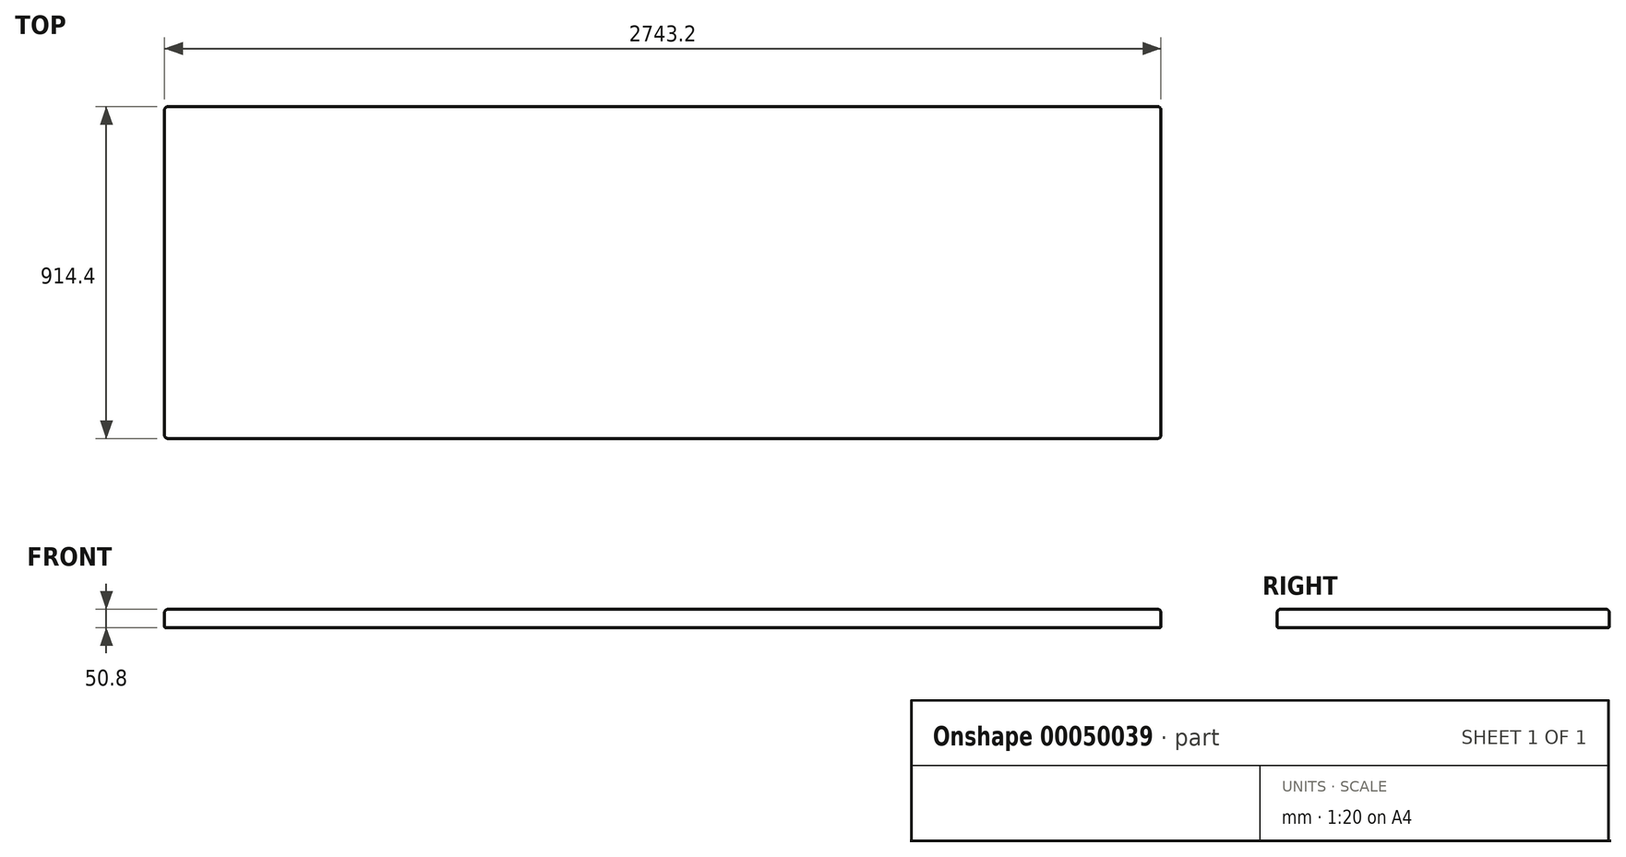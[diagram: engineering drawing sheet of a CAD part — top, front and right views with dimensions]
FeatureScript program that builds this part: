
annotation { "Feature Type Name" : "Feature", "Feature Type Description" : "" }
export const myFeature = defineFeature(function(context is Context, id is Id, definition is map)
    precondition{}
    {
        {
            var Q0;
            Q0=qCreatedBy(makeId("Top.planeOp"),FACE);
            var sketch = newSketch(context, id + "F0", { "sketchPlane" : qUnion([Q0])});
            skLineSegment(sketch, "E0.rect.bottom", {"start": v(1371.6, 457.2) * mm, "end": v(-1371.6, 457.2) * mm});
            skLineSegment(sketch, "E0.rect.top", {"start": v(1371.6, -457.2) * mm, "end": v(-1371.6, -457.2) * mm});
            skLineSegment(sketch, "E0.rect.left", {"start": v(1371.6, 457.2) * mm, "end": v(1371.6, -457.2) * mm});
            skLineSegment(sketch, "E0.rect.right", {"start": v(-1371.6, 457.2) * mm, "end": v(-1371.6, -457.2) * mm});
            skPoint(sketch, "E0.rect.middle", {"position": v(0, 0) * mm});
            skSolve(sketch);
        }
        {
            var Q0;
            Q0=makeQuery(id+"F0.imprint","IMPRINT",FACE,{"disambiguationData":[TD([[makeQuery(id+"F0.imprint","IMPRINT",EDGE,{"derivedFrom":sQuery(id+"F0.wireOp",EDGE,"E0.rect.bottom")}),1.0]])]});
            extrude(context, id + "F1", {"entities" : qUnion([Q0]), "depth" : 50.8 * mm});
        }
        {
            var Q0;
            Q0=makeQuery(id+"F1.opExtrude","CAP_EDGE",EDGE,{"disambiguationData":[OSD([sQuery(id+"F0.wireOp",EDGE,"E0.rect.bottom")])],"isStart":false});
            var Q1;
            Q1=makeQuery(id+"F1.opExtrude","CAP_EDGE",EDGE,{"disambiguationData":[OSD([sQuery(id+"F0.wireOp",EDGE,"E0.rect.left")])],"isStart":false});
            var Q2;
            Q2=makeQuery(id+"F1.opExtrude","CAP_EDGE",EDGE,{"disambiguationData":[OSD([sQuery(id+"F0.wireOp",EDGE,"E0.rect.top")])],"isStart":false});
            var Q3;
            Q3=makeQuery(id+"F1.opExtrude","CAP_EDGE",EDGE,{"disambiguationData":[OSD([sQuery(id+"F0.wireOp",EDGE,"E0.rect.right")])],"isStart":false});
            fillet(context, id + "F2", {"entities" : qUnion([Q0, Q1, Q2, Q3]), "radius" : 9.52 * mm, "tangentPropagation" : true, "allowEdgeOverflow" : false});
        }
        {
            var Q0;
            Q0=makeQuery(id+"F1.opExtrude","SWEPT_EDGE",EDGE,{"disambiguationData":[OSD([sQuery(id+"F0.wireOp",EDGE,"E0.rect.top"),sQuery(id+"F0.wireOp",EDGE,"E0.rect.left")])]});
            var Q1;
            Q1=makeQuery(id+"F1.opExtrude","SWEPT_EDGE",EDGE,{"disambiguationData":[OSD([sQuery(id+"F0.wireOp",EDGE,"E0.rect.bottom"),sQuery(id+"F0.wireOp",EDGE,"E0.rect.left")])]});
            fillet(context, id + "F3", {"entities" : qUnion([Q0, Q1]), "radius" : 9.52 * mm, "tangentPropagation" : true, "allowEdgeOverflow" : false});
        }
        {
            var Q0;
            Q0=makeQuery(id+"F1.opExtrude","CAP_EDGE",EDGE,{"disambiguationData":[OSD([sQuery(id+"F0.wireOp",EDGE,"E0.rect.right")])],"isStart":true});
            var Q1;
            Q1=makeQuery(id+"F1.opExtrude","CAP_EDGE",EDGE,{"disambiguationData":[OSD([sQuery(id+"F0.wireOp",EDGE,"E0.rect.top")])],"isStart":true});
            var Q2;
            Q2=makeQuery(id+"F1.opExtrude","CAP_EDGE",EDGE,{"disambiguationData":[OSD([sQuery(id+"F0.wireOp",EDGE,"E0.rect.left")])],"isStart":true});
            var Q3;
            Q3=makeQuery(id+"F1.opExtrude","CAP_EDGE",EDGE,{"disambiguationData":[OSD([sQuery(id+"F0.wireOp",EDGE,"E0.rect.bottom")])],"isStart":true});
            fillet(context, id + "F4", {"entities" : qUnion([Q0, Q1, Q2, Q3]), "radius" : 3.17 * mm, "tangentPropagation" : true, "allowEdgeOverflow" : false});
        }
        {
            var Q0;
            Q0=makeQuery(id+"F1.opExtrude","SWEPT_EDGE",EDGE,{"disambiguationData":[OSD([sQuery(id+"F0.wireOp",EDGE,"E0.rect.bottom"),sQuery(id+"F0.wireOp",EDGE,"E0.rect.right")])]});
            var Q1;
            Q1=makeQuery(id+"F1.opExtrude","SWEPT_EDGE",EDGE,{"disambiguationData":[OSD([sQuery(id+"F0.wireOp",EDGE,"E0.rect.top"),sQuery(id+"F0.wireOp",EDGE,"E0.rect.right")])]});
            fillet(context, id + "F5", {"entities" : qUnion([Q0, Q1]), "radius" : 9.52 * mm, "tangentPropagation" : true, "allowEdgeOverflow" : false});
        }
    });
